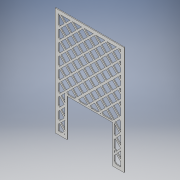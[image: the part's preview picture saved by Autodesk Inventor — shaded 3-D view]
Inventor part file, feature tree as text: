
AUTODESK INVENTOR PART (.ipt)
format: ipt  version: 2017 (Build 210142000, 142)  size: 532,992 bytes
history: native  units: in
note: dims shown in document units (in); Inventor stores cm internally (conversion verified against a paired STEP export)
features: extrude x1, sketch x1
ambient origin geometry x8: Origin, YZ Plane, XZ Plane, XY Plane, X Axis, Y Axis, Z Axis, Center Point
bodies: Body1 (feature_tree)
feature tree (2):
  extrude  "Extrusion2"  Depth=33.0in
  sketch  "Sketch1"  dims[d0=21.0in d1=33.0in d2=1.0in d3=45.0deg d4=0.5in d5=2.0in d6=0.5in d7=2.0in d8=0.5in d9=2.0in d10=0.5in d11=2.0in d12=0.5in d13=2.0in d14=0.5in d15=2.0in d16=0.5in d18=2.0in d19=0.5in d20=2.0in d23=0.5in d24=2.0in d25=0.5in d26=2.0in d27=0.0034in d28=2.0in d29=0.5in d30=2.0in d31=0.5in d32=0.5in d33=0.5in d34=2.0in d37=3.0in d38=3.0in d39=12.0in d40=0.25in d41=0.0in]
